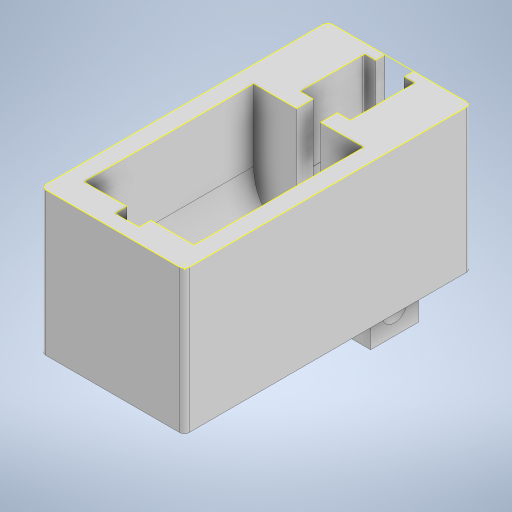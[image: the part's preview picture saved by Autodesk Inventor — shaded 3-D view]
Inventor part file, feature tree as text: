
AUTODESK INVENTOR PART (.ipt)
format: ipt  version: 2023 (Build 270158000, 158)  size: 937,472 bytes
history: native  units: in
note: dims shown in document units (in); Inventor stores cm internally (conversion verified against a paired STEP export)
features: extrude x17, sketch x15, plane x9, projected_geometry x4, fillet x3, chamfer x3
ambient origin geometry x8: Origin, YZ Plane, XZ Plane, XY Plane, X Axis, Y Axis, Z Axis, Center Point
bodies: Solid1 (feature_tree)
feature tree (51):
  sketch  "Sketch1"  dims[d0=2.3622in d1=4.7244in d2=1.7717in d3=0.1969in d4=0.9843in d5=0.0394in d6=0.4921in d7=0.3937in d8=0.0984in d9=0.8858in d10=-2.7165in d11=0.9843in d12=90.0deg d13=0.8268in d14=0.1969in d15=0.3937in d16=90.0deg d17=0.3937in d18=-2.7165in d19=90.0deg d20=-1.3583in d21=1.7717in d22=2.3622in d23=0.0in]
  extrude  "Extrusion1"  Depth=2.3622in TaperAngle=0.0deg
  sketch  "Sketch2"  dims[d24=-0.1969in d25=0.8268in]
  plane  "Work Plane1"
  plane  "Work Plane2"
  plane  "Work Plane3"
  plane  "Work Plane5"
  sketch  "Sketch3"  dims[d28=0.3937in d29=0.0in d30=0.3937in]
  plane  "Work Plane6"
  extrude  "Extrusion3"  Depth=0.8268in
  sketch  "Sketch4"  dims[d31=1.811in d32=0.3937in d33=0.0in]
  sketch  "Sketch5"  dims[d34=0.3937in d35=0.0in d36=0.3937in d37=0.0in]
  extrude  "Extrusion4"  Depth=0.3937in
  plane  "Work Plane7"
  extrude  "Extrusion5"  Depth=0.3937in TaperAngle=0.0deg
  extrude  "Extrusion6"  Depth=0.3937in TaperAngle=0.0deg
  extrude  "Extrusion7"  Depth=0.3937in TaperAngle=0.0deg
  fillet  "Fillet1"  Radius=0.0787in
  extrude  "Extrusion8"  Depth=0.3937in
  chamfer  "Chamfer1"  [1 undecoded]
  chamfer  "Chamfer2"  Distance=0.0787in Angle=45.0deg
  fillet  "Fillet2"  Radius=0.0394in
  fillet  "Fillet3"  Radius=0.0394in
  extrude  "Extrusion11"  Depth=0.3937in
  extrude  "Extrusion12"  Depth=0.3937in
  extrude  "Extrusion13"  Depth=0.3937in TaperAngle=0.0deg
  chamfer  "Chamfer3"  [1 undecoded]
  plane  "Work Plane8"
  extrude  "Extrusion14"  Depth=0.0787in
  extrude  "Extrusion15"  Depth=0.1969in
  extrude  "Extrusion16"  Depth=0.3937in TaperAngle=0.0deg
  extrude  "Extrusion17"  Depth=0.3937in
  extrude  "Extrusion19"  Depth=0.2362in
  extrude  "Extrusion20"  Depth=0.3937in TaperAngle=0.0deg
  plane  "Work Plane9"
  extrude  "Extrusion21"  Depth=0.1969in TaperAngle=0.0deg
  sketch  "Sketch17"  dims[d90=0.1575in d91=0.7874in d92=0.0in d93=0.481in d95=0.2362in d96=0.6299in d97=0.0in d98=0.1969in d99=0.0in d100=0.0197in d101=0.0197in d102=0.1969in d103=0.0in d104=0.0787in d107=0.3937in d108=0.0in d112=0.0394in d113=0.0394in d114=0.0394in d115=0.0394in d116=0.0in d117=0.0in d118=-0.0394in d119=0.3937in d120=0.0in]
  projected_geometry  "Projected Loop1"
  plane  "Work Plane4"
  sketch  "Sketch7"  dims[d38=-0.0787in d39=0.3937in d40=0.0in d41=0.0787in]
  sketch  "Sketch8"  dims[d42=0.3937in d43=0.3937in d44=0.0in d45=0.0in d46=0.0787in d47=0.0787in d48=45.0deg]
  sketch  "Sketch9"  dims[d49=0.0787in d50=0.0787in d51=45.0deg d52=0.0394in d53=0.0394in]
  sketch  "Sketch11"  dims[d69=0.3937in d70=0.0in d72=0.315in]
  sketch  "Sketch12"  dims[d74=0.7874in d75=0.3937in]
  sketch  "Sketch13"  dims[d76=0.3937in d79=0.7874in d80=0.0in]
  sketch  "Sketch14"  dims[d81=0.2559in d82=0.0in d83=0.0in]
  sketch  "Sketch15"  dims[d84=0.0787in d85=0.0787in d86=45.0deg d87=0.6299in]
  projected_geometry  "Projected Loop3"
  sketch  "Sketch16"  dims[d88=-1.1811in d89=0.1969in]
  projected_geometry  "Projected Loop4"
  projected_geometry  "Projected Loop5"
note: 2 required parameter values undecoded (feature->parameter linkage not recoverable at this tier; creation-order binding heuristic only, values carry confidence <= 0.55)
